# Revit family: ARGOPRO-1500-LP_AUB02320860001
name_source: partatom
category: Lighting Fixtures
units: mm (PartAtom-declared; Revit-internal decimal feet)

## family parameters
Cut with Voids When Loaded = No
Host = Face
Light Source = Yes
Part Type = Normal
Room Calculation Point = No
Round Connector Dimension = Use Diameter
Shared = No

## types (1)
- ARGOPRO-1500-LP_AUB02320860001
    Apparent Load = 54 VA
    Clevertronics_240V Driver = 1330072 - LED Driver - Tridonic LC 75W 900–1800mA flexC lp EXC
    Clevertronics_240V LED Strip = 8002756 - PCA:LED Strip ARGOPRO-1500,HT10540-A1,20P16S,4000K
    Clevertronics_AS2293 Classification = C0=D63 C90=D40
    Clevertronics_Annotation Size = 0 mm  [stored 0 ft]
    Clevertronics_Applicable Standards = AS/NZS3820, CISPR15, AS/NZS2293.3
    Clevertronics_Battery = Lithium Iron Phosphate
    Clevertronics_Battery Type = 3.2V 6400mAh
    Clevertronics_Charging Method = Intelligent current limited constant voltage
    Clevertronics_Construction = Polycarbonate Base and Diffuser w/Stainless Steel Clips (SS316)
    Clevertronics_Diffuser = Polycarbonate
    Clevertronics_Dimensions Main Enclosure = 1565x160x105
    Clevertronics_Driver/Ballast = LED Driver - Tridonic LC 75W 900–1800mA flexC lp EXC
    Clevertronics_EM LED Strip = 8003110 - PCA: Batten EM Class HT10582-Ax 1S4P
    Clevertronics_Earth Leakage = 0.49mA
    Clevertronics_Emergency Driver = AUM02370050001 - Lifelight Pro, Control Only, 530mm, NP, CTP, OWC
    Clevertronics_Height = 105 mm  [stored 0.344488 ft]
    Clevertronics_IK Rating = IK08
    Clevertronics_IP Rating = IP65
    Clevertronics_Inrush Current (MAX) = 40.4A<800μs
    Clevertronics_Length = 1565 mm  [stored 5.13451 ft]
    Clevertronics_MIC Number = AUB02320860001
    Clevertronics_Material = Clevertronics_Plycarbonate Base
    Clevertronics_Mounting = Surface Mount
    Clevertronics_Operating Mode = Sustained
    Clevertronics_Operating Temperature = 0ºC to 40ºC
    Clevertronics_Operating Voltage = 220-240V~ 50Hz
    Clevertronics_Output Configuration = Configurable Dual Output
    Clevertronics_Power Factor = 0.92
    Clevertronics_Product Description = Argonaut Pro 1500mm Weatherproof Emergency Batten, LP, Clevertest Plus
    Clevertronics_Replacement Battery = 1550230 - BATT:LP 3.2V 6400mAh.200mm lead.Brkt.
    Clevertronics_Supply Current = 215mA +/-20mA
    Clevertronics_Testing System = Clevertest Plus Enabled (not activated by default)
    Clevertronics_Total Lumen Output = 6358 lm
    Clevertronics_Weight = 3.6 Kg
    Clevertronics_Width = 160 mm  [stored 0.524934 ft]
    Color Filter = 16777215
    Default Elevation = 1200 mm
    Description = Argonaut Pro 1500mm Weatherproof Emergency Batten, LP, Clevertest Plus
    Dimming Lamp Color Temperature Shift = <None>
    Lamp = LED strip module, 4000K, Ra>80// L70/B50 Ta 40ºC; LM80 Report >60,000hr, Projected 184,000hr//L80/B20 Ta 40ºC; LM80 Report >60,000hr, Projected 100,000hr//L90/B10 Ta 40ºC; LM80 Report 43,000hr, Projected 43,000hr
    Manufacturer = Clevertronics
    Model = ARGOPRO-1500-LP
    Photometric Web File = ARGOPRO-1500-LP_IESR_E_693-8_20210224.ies
    Tilt Angle = -90.00°
    URL = https://clevertronics.com.au

note: [stored X ft] marks values corroborated as IEEE doubles in the binary element streams (Revit-internal decimal feet)

## geometry (parser evidence)
native form markers: Blend x2, Sweep x1
no freeform markers — native parametric forms only
